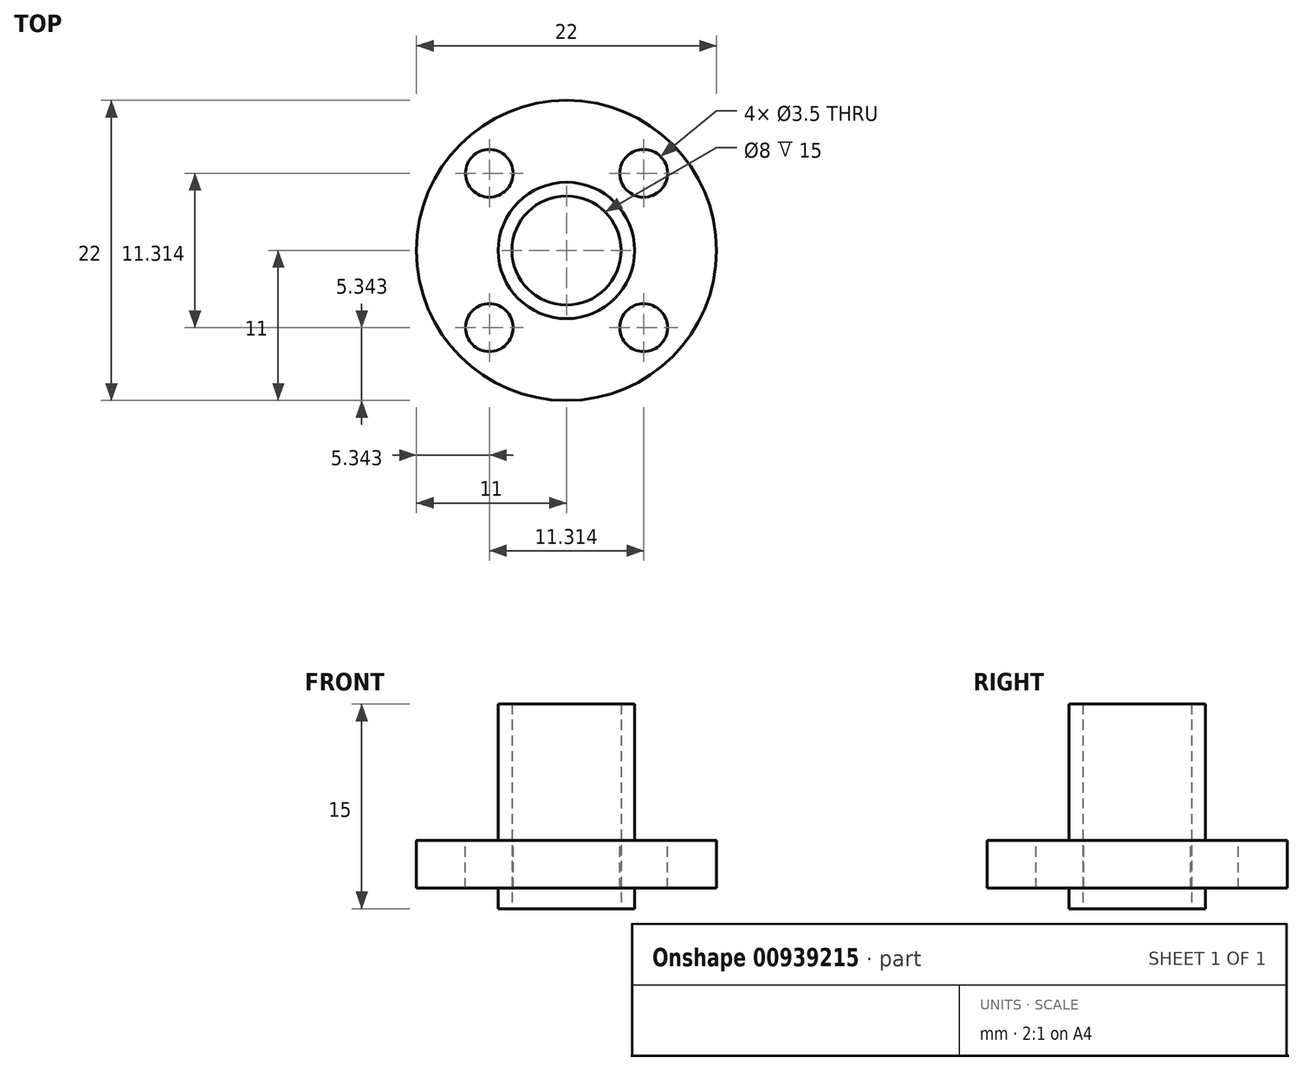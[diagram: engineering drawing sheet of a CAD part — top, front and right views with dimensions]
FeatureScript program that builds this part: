
annotation { "Feature Type Name" : "Feature", "Feature Type Description" : "" }
export const myFeature = defineFeature(function(context is Context, id is Id, definition is map)
    precondition{}
    {
        {
            var Q0;
            Q0=qCreatedBy(makeId("Top.planeOp"),FACE);
            var sketch = newSketch(context, id + "F0", { "sketchPlane" : qUnion([Q0])});
            skCircle(sketch, "E0", {"center": v(0, 0) * mm, "radius": 4 * mm});
            skCircle(sketch, "E1", {"center": v(0, 0) * mm, "radius": 5 * mm});
            skCircle(sketch, "E2", {"center": v(0, 0) * mm, "radius": 11 * mm});
            skCircle(sketch, "E3", {"center": v(0, 0) * mm, "radius": 8 * mm, "construction": true});
            skLineSegment(sketch, "E4.bottom", {"start": v(5.66, 5.66) * mm, "end": v(-5.66, 5.66) * mm, "construction": true});
            skLineSegment(sketch, "E4.top", {"start": v(5.66, -5.66) * mm, "end": v(-5.66, -5.66) * mm, "construction": true});
            skLineSegment(sketch, "E4.left", {"start": v(5.66, 5.66) * mm, "end": v(5.66, -5.66) * mm, "construction": true});
            skLineSegment(sketch, "E4.right", {"start": v(-5.66, 5.66) * mm, "end": v(-5.66, -5.66) * mm, "construction": true});
            skSolve(sketch);
        }
        {
            var Q0;
            Q0=makeQuery(id+"F0.imprint","IMPRINT",FACE,{"disambiguationData":[TD([[makeQuery(id+"F0.imprint","IMPRINT",EDGE,{"derivedFrom":sQuery(id+"F0.wireOp",EDGE,"E0")}),-1.0]])]});
            extrude(context, id + "F1", {"entities" : qUnion([Q0]), "depth" : 10 * mm, "offsetDistance" : 25 * mm});
        }
        {
            var Q0;
            Q0=makeQuery(id+"F0.imprint","IMPRINT",FACE,{"disambiguationData":[TD([[makeQuery(id+"F0.imprint","IMPRINT",EDGE,{"derivedFrom":sQuery(id+"F0.wireOp",EDGE,"E0")}),-1.0]])]});
            extrude(context, id + "F2", {"entities" : qUnion([Q0]), "operationType" : NewBodyOperationType.ADD, "oppositeDirection" : true, "depth" : 5 * mm, "offsetDistance" : 25 * mm});
        }
        {
            var Q0;
            Q0=makeQuery(id+"F0.imprint","IMPRINT",FACE,{"disambiguationData":[TD([[makeQuery(id+"F0.imprint","IMPRINT",EDGE,{"derivedFrom":sQuery(id+"F0.wireOp",EDGE,"E1")}),-1.0]])]});
            extrude(context, id + "F3", {"entities" : qUnion([Q0]), "operationType" : NewBodyOperationType.ADD, "oppositeDirection" : true, "depth" : 3.5 * mm, "offsetDistance" : 25 * mm});
        }
        {
            var Q0;
            Q0=sQuery(id+"F0.wireOp",VERTEX,"E4.bottom.end");
            var Q1;
            Q1=sQuery(id+"F0.wireOp",VERTEX,"E4.bottom.start");
            var Q2;
            Q2=sQuery(id+"F0.wireOp",VERTEX,"E4.top.start");
            var Q3;
            Q3=sQuery(id+"F0.wireOp",VERTEX,"E4.top.end");
            var Q4;
            Q4=makeQuery(id+"F1.opExtrude","SWEPT_BODY",BODY,{"disambiguationData":[OSD([sQuery(id+"F0.wireOp",EDGE,"E0"),sQuery(id+"F0.wireOp",EDGE,"E1")])]});
            hole(context, id + "F4", {"style" : HoleStyle.SIMPLE, "endStyle" : HoleEndStyle.THROUGH, "holeDiameter" : 3.5 * mm, "majorDiameter" : 5 * mm, "isTappedThrough" : true, "tappedDepth" : 12 * mm, "tapClearance" : 3, "locations" : qUnion([Q0, Q1, Q2, Q3]), "scope" : qUnion([Q4])});
        }
    });
